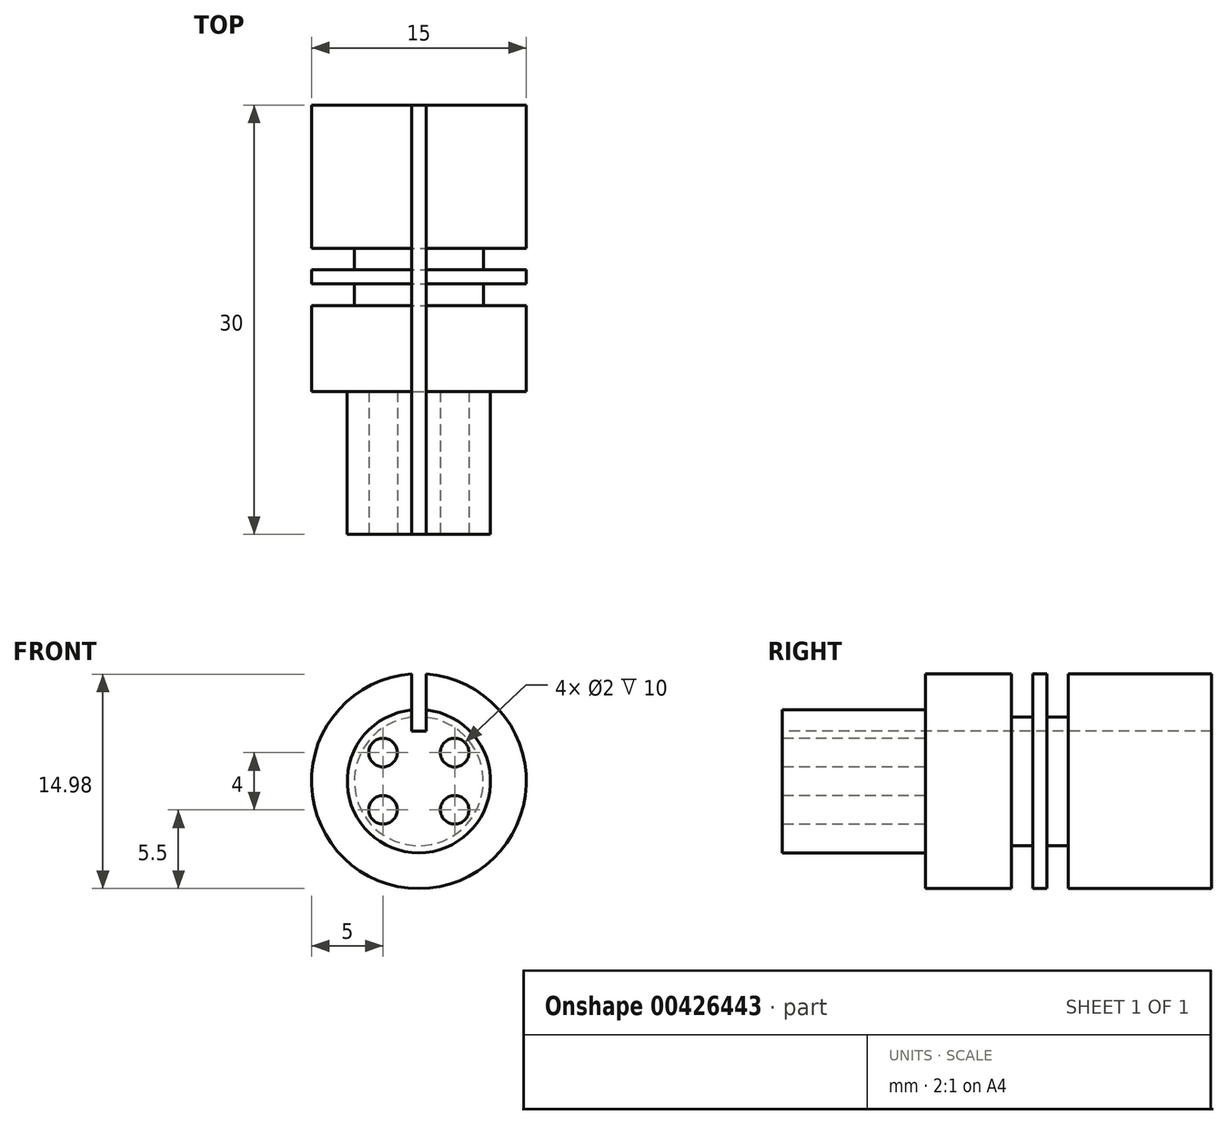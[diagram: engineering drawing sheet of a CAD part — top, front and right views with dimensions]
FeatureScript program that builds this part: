
annotation { "Feature Type Name" : "Feature", "Feature Type Description" : "" }
export const myFeature = defineFeature(function(context is Context, id is Id, definition is map)
    precondition{}
    {
        {
            var Q0;
            Q0=qCreatedBy(makeId("Right.planeOp"),FACE);
            var sketch = newSketch(context, id + "F0", { "sketchPlane" : qUnion([Q0])});
            skLineSegment(sketch, "E0.top", {"start": v(-0.3, 7.5) * mm, "end": v(5.7, 7.5) * mm});
            skLineSegment(sketch, "E0.left", {"start": v(-10.3, 0) * mm, "end": v(-10.3, 5) * mm});
            skLineSegment(sketch, "E1", {"start": v(9.7, 7.5) * mm, "end": v(9.7, 4.5) * mm});
            skLineSegment(sketch, "E2", {"start": v(9.7, 4.5) * mm, "end": v(8.2, 4.5) * mm});
            skLineSegment(sketch, "E3", {"start": v(8.2, 4.5) * mm, "end": v(8.2, 7.5) * mm});
            skLineSegment(sketch, "E4", {"start": v(7.2, 7.5) * mm, "end": v(7.2, 4.5) * mm});
            skLineSegment(sketch, "E5", {"start": v(7.2, 4.5) * mm, "end": v(5.7, 4.5) * mm});
            skLineSegment(sketch, "E6", {"start": v(5.7, 4.5) * mm, "end": v(5.7, 7.5) * mm});
            skLineSegment(sketch, "E7.trimOffspring", {"start": v(7.2, 7.5) * mm, "end": v(8.2, 7.5) * mm});
            skLineSegment(sketch, "E8.trimOffspring", {"start": v(9.7, 7.5) * mm, "end": v(9.7, 7.5) * mm});
            skLineSegment(sketch, "E9", {"start": v(9.7, 7.5) * mm, "end": v(19.7, 7.5) * mm});
            skLineSegment(sketch, "E10", {"start": v(-10.3, 5) * mm, "end": v(-0.3, 5) * mm});
            skLineSegment(sketch, "E11", {"start": v(-0.3, 5) * mm, "end": v(-0.3, 7.5) * mm});
            skLineSegment(sketch, "E12", {"start": v(19.7, 7.5) * mm, "end": v(19.7, 0) * mm});
            skLineSegment(sketch, "E13", {"start": v(-10.3, 0) * mm, "end": v(19.7, 0) * mm});
            skLineSegment(sketch, "E14", {"start": v(-25, 0) * mm, "end": v(50.56, 0) * mm, "construction": true});
            skSolve(sketch);
        }
        {
            var Q0;
            Q0=makeQuery(id+"F0.imprint","IMPRINT",FACE,{"disambiguationData":[TD([[makeQuery(id+"F0.imprint","IMPRINT",EDGE,{"derivedFrom":sQuery(id+"F0.wireOp",EDGE,"E0.top")}),-1.0]])]});
            var Q1;
            Q1=sQuery(id+"F0.wireOp",EDGE,"E14");
            revolve(context, id + "F1", {"entities" : qUnion([Q0]), "axis" : qUnion([Q1]), "revolveType" : RevolveType.FULL});
        }
        {
            var Q0;
            Q0=makeQuery(id+"F1.opRevolve","SWEPT_FACE",FACE,{"disambiguationData":[OSD([sQuery(id+"F0.wireOp",EDGE,"E0.left")])]});
            var sketch = newSketch(context, id + "F2", { "sketchPlane" : qUnion([Q0])});
            skCircle(sketch, "E15", {"center": v(-2.5, 2) * mm, "radius": 1 * mm});
            skLineSegment(sketch, "E16", {"start": v(0, 12.79) * mm, "end": v(0, -16.6) * mm, "construction": true});
            skLineSegment(sketch, "E17", {"start": v(-19.05, 0) * mm, "end": v(18.94, 0) * mm, "construction": true});
            skCircle(sketch, "E18.MirrorC", {"center": v(2.5, 2) * mm, "radius": 1 * mm});
            skLineSegment(sketch, "E19.MirrorCS", {"start": v(19.05, 0) * mm, "end": v(-18.94, 0) * mm, "construction": true});
            skCircle(sketch, "E20.MirrorC", {"center": v(-2.5, -2) * mm, "radius": 1 * mm});
            skCircle(sketch, "E21.MirrorC", {"center": v(2.5, -2) * mm, "radius": 1 * mm});
            skSolve(sketch);
        }
        {
            var Q0;
            Q0=qSketchRegion(id+"F2",true);
            extrude(context, id + "F3", {"entities" : qUnion([Q0]), "operationType" : NewBodyOperationType.REMOVE, "oppositeDirection" : true, "depth" : 10 * mm});
        }
        {
            var Q0;
            Q0=makeQuery(id+"F1.opRevolve","SWEPT_FACE",FACE,{"disambiguationData":[OSD([sQuery(id+"F0.wireOp",EDGE,"E0.left")])]});
            var sketch = newSketch(context, id + "F4", { "sketchPlane" : qUnion([Q0])});
            skLineSegment(sketch, "E22.bottom", {"start": v(0, 7.5) * mm, "end": v(-0.5, 7.5) * mm});
            skLineSegment(sketch, "E22.top", {"start": v(0, 3.5) * mm, "end": v(-0.5, 3.5) * mm});
            skLineSegment(sketch, "E22.left", {"start": v(0, 7.5) * mm, "end": v(0, 3.5) * mm});
            skLineSegment(sketch, "E22.right", {"start": v(-0.5, 7.5) * mm, "end": v(-0.5, 3.5) * mm});
            skLineSegment(sketch, "E23.bottom", {"start": v(0, 7.5) * mm, "end": v(0.5, 7.5) * mm});
            skLineSegment(sketch, "E23.top", {"start": v(0, 3.5) * mm, "end": v(0.5, 3.5) * mm});
            skLineSegment(sketch, "E23.right", {"start": v(0.5, 7.5) * mm, "end": v(0.5, 3.5) * mm});
            skSolve(sketch);
        }
        {
            var Q0;
            Q0=qSketchRegion(id+"F4",true);
            extrude(context, id + "F5", {"entities" : qUnion([Q0]), "operationType" : NewBodyOperationType.REMOVE, "endBound" : BoundingType.THROUGH_ALL, "oppositeDirection" : true, "depth" : 20 * mm});
        }
    });
